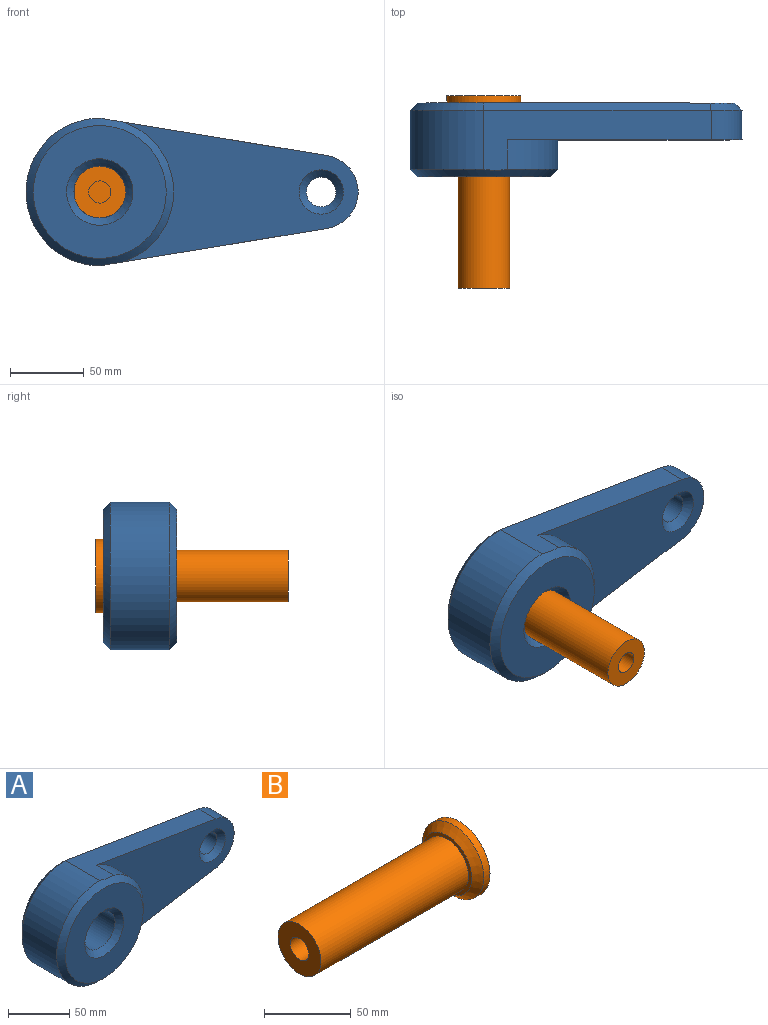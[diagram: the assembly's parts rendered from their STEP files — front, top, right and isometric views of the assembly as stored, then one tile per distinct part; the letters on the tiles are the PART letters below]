
ASSEMBLY  parts=2 mates=1
PART A: 19 faces, bbox 225x50x100 mm
  f0: plane 154.06x40.67mm, normal (0.16,0,0.99), area 3454.2mm2, adj f2,f5,f6,f7,f10,f14
  f1: plane 154.06x40.67mm, normal (0.16,0,-0.99), area 3454.2mm2, adj f2,f5,f6,f7,f13,f14
  f2: cylinder r=25mm len=49.34mm, axis (0,-1,0), area 1407.8mm2, adj f0,f1,f5,f12
  f3: cylinder r=10mm len=20mm, axis (0,-1,0), area 942.5mm2, adj f16,f17
  f4: plane 215x90mm, normal (0,1,0), area 11292.7mm2, adj f10,f11,f12,f13,f15,f17
  f5: plane 158.99x94.74mm, normal (0,-1,0), area 7663.5mm2, adj f0,f1,f2,f6,f16
  f6: cylinder r=50mm len=94.74mm, axis (0,1,0), area 2489.7mm2, adj f0,f1,f5,f14
  f7: cylinder r=50mm len=100mm, axis (0,1,0), area 6283.2mm2, adj f0,f1,f11,f14
  f8: cylinder r=17.5mm len=40mm, axis (0,1,0), area 4398.2mm2, adj f15,f18
  f9: plane 90x90mm, normal (0,-1,0), area 4771.3mm2, adj f14,f18
  f10: plane 154.47x30.28mm, normal (0.11,0.71,0.7), area 1102.5mm2, adj f0,f4,f11,f12
  f11: cone r=50mm half-angle=45deg, axis (0,-1,0), area 1052.3mm2, adj f4,f7,f10,f13
  f12: cone r=25mm half-angle=45deg, axis (0,-1,0), area 448mm2, adj f2,f4,f10,f13
  f13: plane 154.47x30.28mm, normal (0.11,0.71,-0.7), area 1102.5mm2, adj f1,f4,f11,f12
  f14: cone r=45mm half-angle=45deg, axis (0,1,0), area 2090.1mm2, adj f0,f1,f6,f7,f9
  f15: cone r=22.5mm half-angle=45deg, axis (0,1,0), area 888.6mm2, adj f4,f8
  f16: cone r=10mm half-angle=45deg, axis (0,-1,0), area 555.4mm2, adj f3,f5
  f17: cone r=15mm half-angle=45deg, axis (0,1,0), area 555.4mm2, adj f3,f4
  f18: cone r=17.5mm half-angle=45deg, axis (0,-1,0), area 888.6mm2, adj f8,f9
PART B: 8 faces, bbox 130.5x50x50 mm
  f0: cylinder r=17.5mm len=120.54mm, axis (1,0,0), area 13254.5mm2, adj f1,f5
  f1: plane 40x40mm, normal (-1,0,0), area 294.5mm2, adj f0,f4
  f2: cylinder r=25mm len=50mm, axis (1,0,0), area 785.4mm2, adj f3,f4
  f3: plane 50x50mm, normal (1,0,0), area 1963.5mm2, adj f2
  f4: cone r=25mm half-angle=45deg, axis (1,0,0), area 999.6mm2, adj f1,f2
  f5: plane 35x35mm, normal (-1,0,0), area 785.4mm2, adj f0,f7
  f6: plane 15x15mm, normal (-1,0,0), area 176.7mm2, adj f7
  f7: cylinder r=7.5mm len=120.54mm, axis (1,0,0), area 5680.5mm2, adj f5,f6
PLACE A t=(4.72,3.36,-3.51)mm
PLACE B rot(axis=(-0.58,-0.58,0.58),120deg) t=(17.22,15.59,-3.51)mm
MATE fastened B.f0 <-> A.f6  axis (0,1,0) through (4.72,23.36,-3.51)mm
